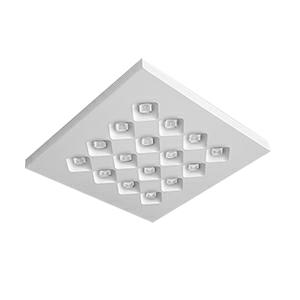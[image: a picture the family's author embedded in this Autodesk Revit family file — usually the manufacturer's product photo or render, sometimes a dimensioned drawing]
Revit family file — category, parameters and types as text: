
# Revit family: 3f_filippi_-_3f_diagon_3f_filippi_-_23122_a0686_-_3f_diagon_25w-940_596x596___corn_plaf__da65
name_source: partatom
category: Lighting Fixtures
units: mm (PartAtom-declared; Revit-internal decimal feet)

## family parameters
Cut with Voids When Loaded = No
Host = Face
Light Source = No
Part Type = Normal
Room Calculation Point = No
Round Connector Dimension = Use Diameter
Shared = No

## types (1)
- 3F Filippi - 3F Dìagon (1 x LED, 3294 lm, 28 W, 4000 K)
    Apparent Load = 28 VA
    Approval mark = CE
    CIE Flux Codes = 67 96 100 100 100
    Color Rendering = 90
    Color Temperature = 4000 K
    Control Gear = Electronic ballast
    Default Elevation = 1800 mm
    Description = ILLUMINOTECHNICAL
Luminous efficiency 100% (DLOR 100%, ULOR 0%).
Initial luminous flux of the luminaire 3294 lm.
Direct symmetric distribution.
Installation Interdistance Transv.D = 1.39 x hu - Long.D = 1.39 x hu.
Average luminance <1500 cd/m² for radial angles >65°.
Tabular UGR (CIE 117 - 4H-8H; S=0.25H; 70/50/20): RUG 16.5 - 16.4.
Beam angle: 93° - 92°.
Luminous efficacy 118 lm/W.
Lifetime (L95/B10): 30000 h. (tq+25°C)
Lifetime (L90/B10): 50000 h. (tq+25°C)
Lifetime (L80/B10): 80000 h. (tq+25°C)
Lifetime (L75/B10): 100000 h. (tq+25°C)
Sudden decreased luminous flux after 50000 hours: 0% (C0).
Photobiological safety in compliance with IEC/TR 62778: RG0 risk exempt, (IEC 62471).
In compliance with IEC/EN 62722-2-1 - IEC/EN 62717 standards.

SOURCE
Squared LED module 25W/940.
Energy efficiency class (UE 2019/2020 - UE 2019/2015): D.
CIE 13.3 Colour rendering index: CRI >90 (R9 >50%).
IES TM-30 Fidelity Index: Rf = 92 Rg = 101.
CCT nominal colour temperature 4000 K.
Colour initial tolerance (MacAdam): SDCM 3.

MECHANICAL
Housing in hot-galvanised steel, painted in white polyester.
Honeycombed diagonal screen in white anti-glare polycarbonate.
Rhomboidal lenses with differentiated surfaces, etched and prismatic to optimise the orientation of the luminous flux, in transparent methacrylate (PMMA).
Luminaire with limited surface temperature. - D - (EN 60598-2-24)
Dimensions: 600x600 mm, height 40 mm. Weight 6.1 kg.
IP43 protection degree for exposed part, IP20 for recessed part.
Mechanical strength to impacts IK06 (1 joule).
Glow-wire test resistance 650°C.

ELECTRICAL
Halogen Free electronic wiring 230V-50/60Hz, power factor 0.95, THD <25%, constant output current, class I, 1 driver.
Power of the luminaire 28 W.
ENEC - CE.
SAFE FLICKER: PstLM=<1 and SVM=<0.4 (IEC TR 61547-1 and IEC TR 63158), to ensure a more comfortable and safe light.
Luminaire compliant with EN 60598-2-22 for power supply from a centralised emergency system CPSS (Central Power Supply System), not incorporated in the luminaire - high risk areas excluded. The default power and flux are 100% in AC and 100% in DC.
Ambient temperature from 0°C to +25°C.
Temperature class T6 max 85°C.
Quick connection.
Relative humidity UR: <85%.

INSTALLATION
Ceiling.
Height only 40 mm.
All accessories dedicated to this product are available on the Catalog and on our website www.3F-Filippi.com.

ACCESSORIES
A0686 - 596x596 Diagon frame for Ceiling installation.

APPLICATIONS
Environments: staterooms, with VDTs, offices.
Environments with exacting visual tasks, where diffused soft light for optimum visual comfort is required.

WARNING
Luminaire designed for disposal/recycling at end-of-life.
Replaceable (LED only) light source by a professional. Replaceable control gear by a professional.
    Height = 0 mm  [stored 0 ft]
    Lamp = 1 x LED
    Lamp Light Flux = 3294 lm
    Lamp Power = 28 W
    Lamp count = 1
    Length = 600 mm
    Lifetime = 50000 h
    Luminous efficacy = 118 lm/W
    Manufacturer = 3F Filippi
    ModVariant = No
    Model = 3F Filippi - 23122+A0686 - 3F Diagon 25W-940 596x596 + Corn.plaf.
    Mounting Place = Ceiling
    Mounting Type = Recessed
    Number of Poles = 1
    OnlyDefault = Yes
    Power Factor = 1
    Product Name = 3F Filippi - 3F Dìagon
    Product group = recessed luminaire
    ProductGroupID = 4
    Protection Class = Protection class I
    Protection Degree = IP 20
    RLX_Detail_Level = 1
    RLX_Emergency_Light_Flux = 0 lm
    RLX_Emergency_Type = 0
    RLX_Emergency_Type_DB = No
    RlxData = <blob elided: 96165 chars, md5=8b5f8641>
    Socket = socket
    Standby Power = 0 W
    System Light Flux = 3294 lm
    System Power = 28 W
    Type Comments = Product without accessories
    Type Image = 3ffilippi_3f_diagon__a0686.jpg
    URL = http://relux.com
    VarID = ---
    Voltage = 0 V
    Weight = 0.00 kg
    Width = 600 mm

note: [stored X ft] marks values corroborated as IEEE doubles in the binary element streams (Revit-internal decimal feet)

## geometry (parser evidence)
native form markers: Blend x4, Sweep x9
no freeform markers — native parametric forms only
